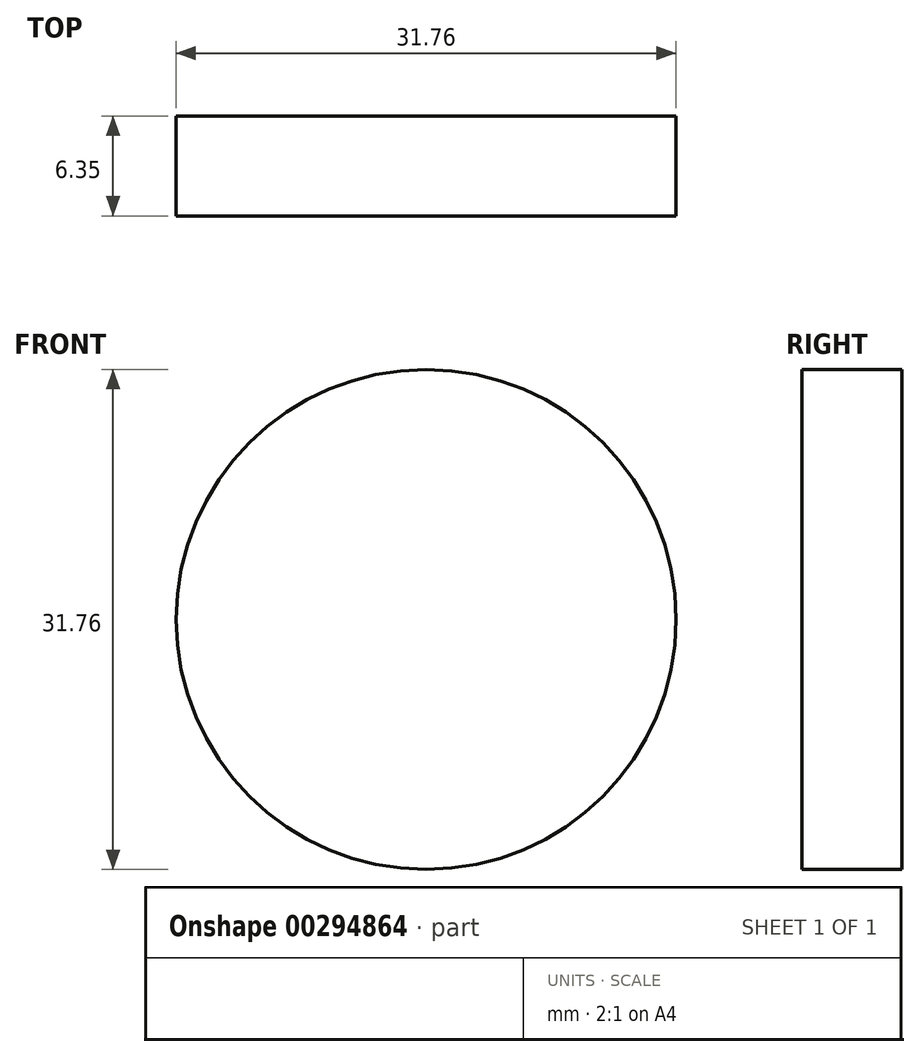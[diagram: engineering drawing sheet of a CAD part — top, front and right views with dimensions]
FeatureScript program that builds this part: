
annotation { "Feature Type Name" : "Feature", "Feature Type Description" : "" }
export const myFeature = defineFeature(function(context is Context, id is Id, definition is map)
    precondition{}
    {
        {
            var Q0;
            Q0=qCreatedBy(makeId("Front.planeOp"),FACE);
            var sketch = newSketch(context, id + "F0", { "sketchPlane" : qUnion([Q0])});
            skCircle(sketch, "E0", {"center": v(0, 0) * mm, "radius": 15.88 * mm});
            skSolve(sketch);
        }
        {
            var Q0;
            Q0=makeQuery(id+"F0.imprint","IMPRINT",FACE,{"disambiguationData":[TD([[makeQuery(id+"F0.imprint","IMPRINT",EDGE,{"derivedFrom":sQuery(id+"F0.wireOp",EDGE,"E0")}),1.0]])]});
            extrude(context, id + "F1", {"entities" : qUnion([Q0]), "depth" : 6.35 * mm});
        }
    });
